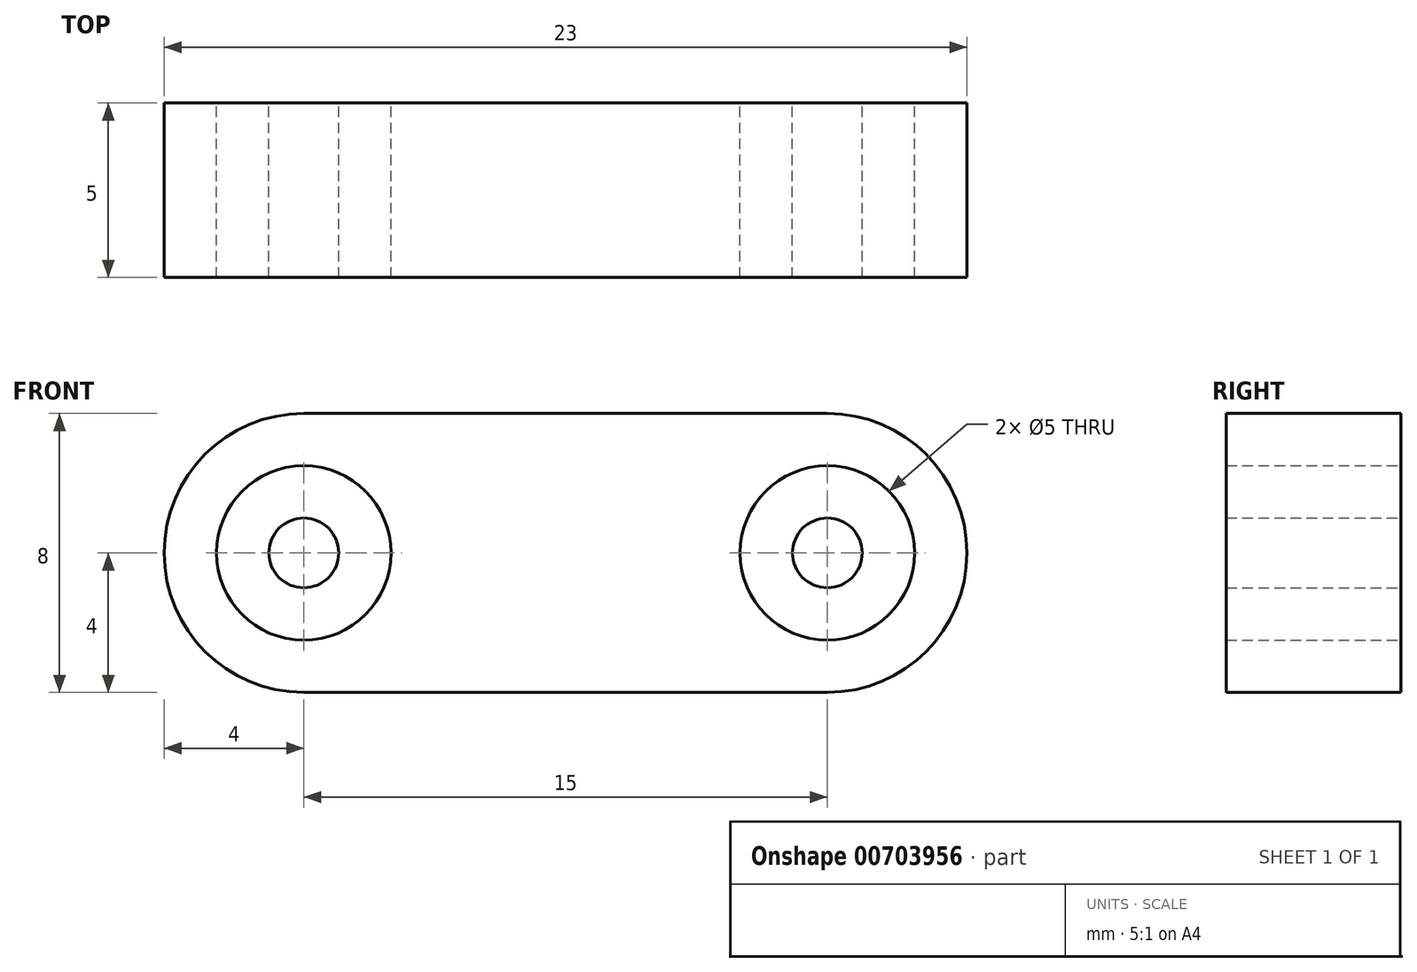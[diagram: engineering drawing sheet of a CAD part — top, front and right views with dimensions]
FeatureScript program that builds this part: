
annotation { "Feature Type Name" : "Feature", "Feature Type Description" : "" }
export const myFeature = defineFeature(function(context is Context, id is Id, definition is map)
    precondition{}
    {
        {
            var Q0;
            Q0=qCreatedBy(makeId("Front.planeOp"),FACE);
            var sketch = newSketch(context, id + "F0", { "sketchPlane" : qUnion([Q0])});
            skCircle(sketch, "E0", {"center": v(0, 0) * mm, "radius": 2.5 * mm});
            skArc(sketch, "E1", {"start": v(0, -4) * mm, "mid": v(-4, 0) * mm, "end": v(0, 4) * mm});
            skCircle(sketch, "E2", {"center": v(15, 0) * mm, "radius": 2.5 * mm});
            skArc(sketch, "E3", {"start": v(15, -4) * mm, "mid": v(19, 0) * mm, "end": v(15, 4) * mm});
            skLineSegment(sketch, "E4", {"start": v(0, 4) * mm, "end": v(15, 4) * mm});
            skLineSegment(sketch, "E5", {"start": v(0, -4) * mm, "end": v(15, -4) * mm});
            skCircle(sketch, "E6", {"center": v(0, 0) * mm, "radius": 1 * mm});
            skCircle(sketch, "E7", {"center": v(15, 0) * mm, "radius": 1 * mm});
            skSolve(sketch);
        }
        {
            var Q0;
            Q0=makeQuery(id+"F0.imprint","IMPRINT",FACE,{"disambiguationData":[TD([[makeQuery(id+"F0.imprint","IMPRINT",EDGE,{"derivedFrom":sQuery(id+"F0.wireOp",EDGE,"E0")}),-1.0]])]});
            var Q1;
            Q1=makeQuery(id+"F0.imprint","IMPRINT",FACE,{"disambiguationData":[TD([[makeQuery(id+"F0.imprint","IMPRINT",EDGE,{"derivedFrom":sQuery(id+"F0.wireOp",EDGE,"E6")}),1.0]])]});
            var Q2;
            Q2=makeQuery(id+"F0.imprint","IMPRINT",FACE,{"disambiguationData":[TD([[makeQuery(id+"F0.imprint","IMPRINT",EDGE,{"derivedFrom":sQuery(id+"F0.wireOp",EDGE,"E7")}),1.0]])]});
            extrude(context, id + "F1", {"entities" : qUnion([Q0, Q1, Q2]), "depth" : 5 * mm, "offsetDistance" : 25 * mm});
        }
    });
